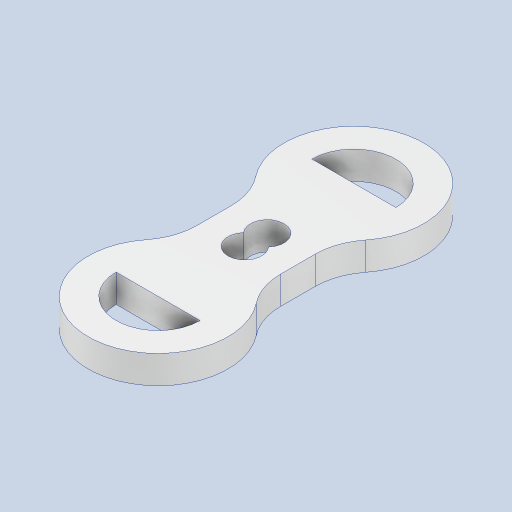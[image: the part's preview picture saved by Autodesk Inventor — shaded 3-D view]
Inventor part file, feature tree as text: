
AUTODESK INVENTOR PART (.ipt)
format: ipt  version: 2024 (Build 280153000, 153)  size: 192,512 bytes
history: native  units: mm
features: extrude x1, sketch x1
ambient origin geometry x8: Origin, YZ Plane, XZ Plane, XY Plane, X Axis, Y Axis, Z Axis, Center Point
bodies: Body1 (feature_tree)
feature tree (2):
  extrude  "Extrusión8"  Depth=10.0mm
  sketch  "Boceto1"  dims[d3=10.0mm d6=0.0mm d29=30.0mm d35=12.0mm d36=12.0mm d37=8.0mm d38=4.0mm d39=10.0mm d40=0.0mm d16=1.0mm d17=1.0mm d18=1.0mm d19=0.15mm d20=0.25mm d21=0.375mm d22=14.3117mm d23=0.75mm d24=20.594885mm d25=0.0625mm d26=0.75mm d27=0.375mm]
